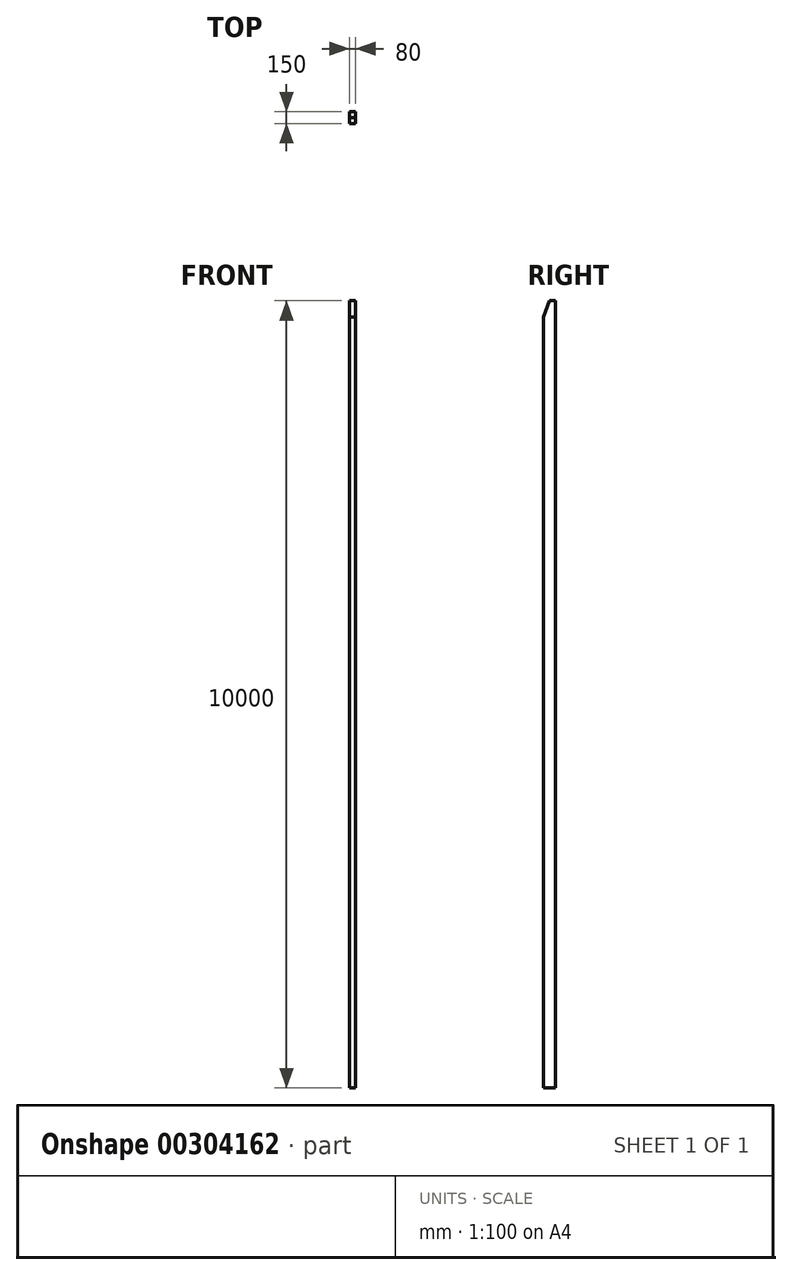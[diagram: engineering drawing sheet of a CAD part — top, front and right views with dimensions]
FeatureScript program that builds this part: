
annotation { "Feature Type Name" : "Feature", "Feature Type Description" : "" }
export const myFeature = defineFeature(function(context is Context, id is Id, definition is map)
    precondition{}
    {
        {
            var Q0;
            Q0=qCreatedBy(makeId("Top.planeOp"),FACE);
            var sketch = newSketch(context, id + "F0", { "sketchPlane" : qUnion([Q0])});
            skLineSegment(sketch, "E0.bottom", {"start": v(-60.93, 41.73) * mm, "end": v(19.07, 41.73) * mm});
            skLineSegment(sketch, "E0.top", {"start": v(-60.93, -108.27) * mm, "end": v(19.07, -108.27) * mm});
            skLineSegment(sketch, "E0.left", {"start": v(-60.93, 41.73) * mm, "end": v(-60.93, -108.27) * mm});
            skLineSegment(sketch, "E0.right", {"start": v(19.07, 41.73) * mm, "end": v(19.07, -108.27) * mm});
            skSolve(sketch);
        }
        {
            var Q0;
            Q0=makeQuery(id+"F0.imprint","IMPRINT",FACE,{"disambiguationData":[TD([[makeQuery(id+"F0.imprint","IMPRINT",EDGE,{"derivedFrom":sQuery(id+"F0.wireOp",EDGE,"E0.bottom")}),-1.0]])]});
            extrude(context, id + "F1", {"entities" : qUnion([Q0]), "depth" : 10000 * mm});
        }
        {
            var Q0;
            Q0=makeQuery(id+"F1.opExtrude","CAP_EDGE",EDGE,{"disambiguationData":[OSD([sQuery(id+"F0.wireOp",EDGE,"E0.top")])],"isStart":false});
            chamfer(context, id + "F2", {"entities" : qUnion([Q0]), "chamferType" : ChamferType.TWO_OFFSETS, "width1" : 75 * mm, "oppositeDirection" : false, "width2" : 210 * mm, "tangentPropagation" : true});
        }
    });
